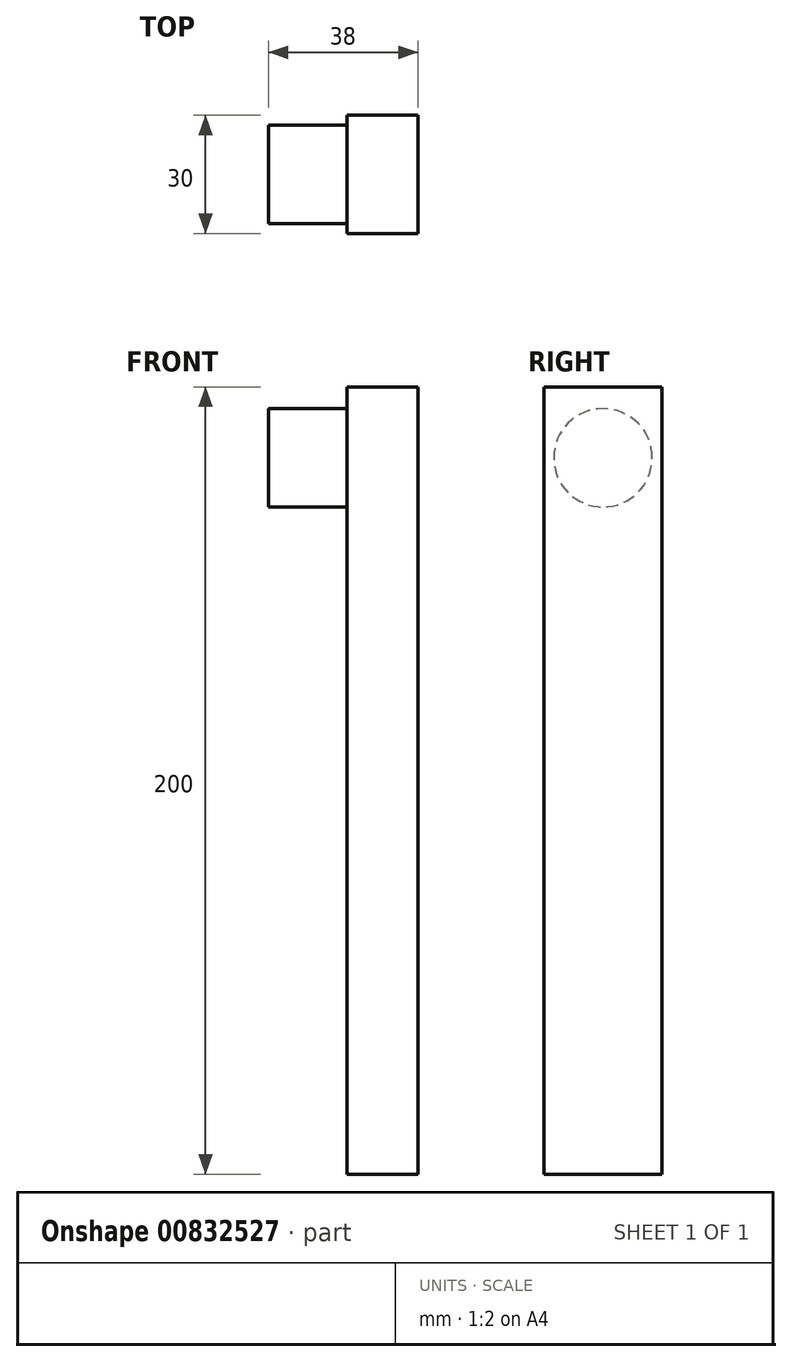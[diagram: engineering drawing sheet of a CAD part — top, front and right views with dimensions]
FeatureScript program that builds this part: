
annotation { "Feature Type Name" : "Feature", "Feature Type Description" : "" }
export const myFeature = defineFeature(function(context is Context, id is Id, definition is map)
    precondition{}
    {
        {
            var Q0;
            Q0=qCreatedBy(makeId("Top.planeOp"),FACE);
            var sketch = newSketch(context, id + "F0", { "sketchPlane" : qUnion([Q0])});
            skLineSegment(sketch, "E0.bottom", {"start": v(-15.3, 27.7) * mm, "end": v(2.7, 27.7) * mm});
            skLineSegment(sketch, "E0.top", {"start": v(-15.3, -2.3) * mm, "end": v(2.7, -2.3) * mm});
            skLineSegment(sketch, "E0.left", {"start": v(-15.3, 27.7) * mm, "end": v(-15.3, -2.3) * mm});
            skLineSegment(sketch, "E0.right", {"start": v(2.7, 27.7) * mm, "end": v(2.7, -2.3) * mm});
            skSolve(sketch);
        }
        {
            var Q0;
            Q0=makeQuery(id+"F0.imprint","IMPRINT",FACE,{"disambiguationData":[TD([[makeQuery(id+"F0.imprint","IMPRINT",EDGE,{"derivedFrom":sQuery(id+"F0.wireOp",EDGE,"E0.bottom")}),-1.0]])]});
            extrude(context, id + "F1", {"entities" : qUnion([Q0]), "depth" : 200 * mm, "offsetDistance" : 25 * mm});
        }
        {
            var Q0;
            Q0=makeQuery(id+"F1.opExtrude","SWEPT_FACE",FACE,{"disambiguationData":[OSD([sQuery(id+"F0.wireOp",EDGE,"E0.left")])]});
            var sketch = newSketch(context, id + "F2", { "sketchPlane" : qUnion([Q0])});
            skCircle(sketch, "E1", {"center": v(-12.7, 182) * mm, "radius": 12.5 * mm});
            skSolve(sketch);
        }
        {
            var Q0;
            Q0=makeQuery(id+"F2.imprint","IMPRINT",FACE,{"disambiguationData":[TD([[makeQuery(id+"F2.imprint","IMPRINT",EDGE,{"derivedFrom":sQuery(id+"F2.wireOp",EDGE,"E1")}),1.0]])]});
            extrude(context, id + "F3", {"entities" : qUnion([Q0]), "operationType" : NewBodyOperationType.ADD, "depth" : 20 * mm, "offsetDistance" : 25 * mm});
        }
    });
